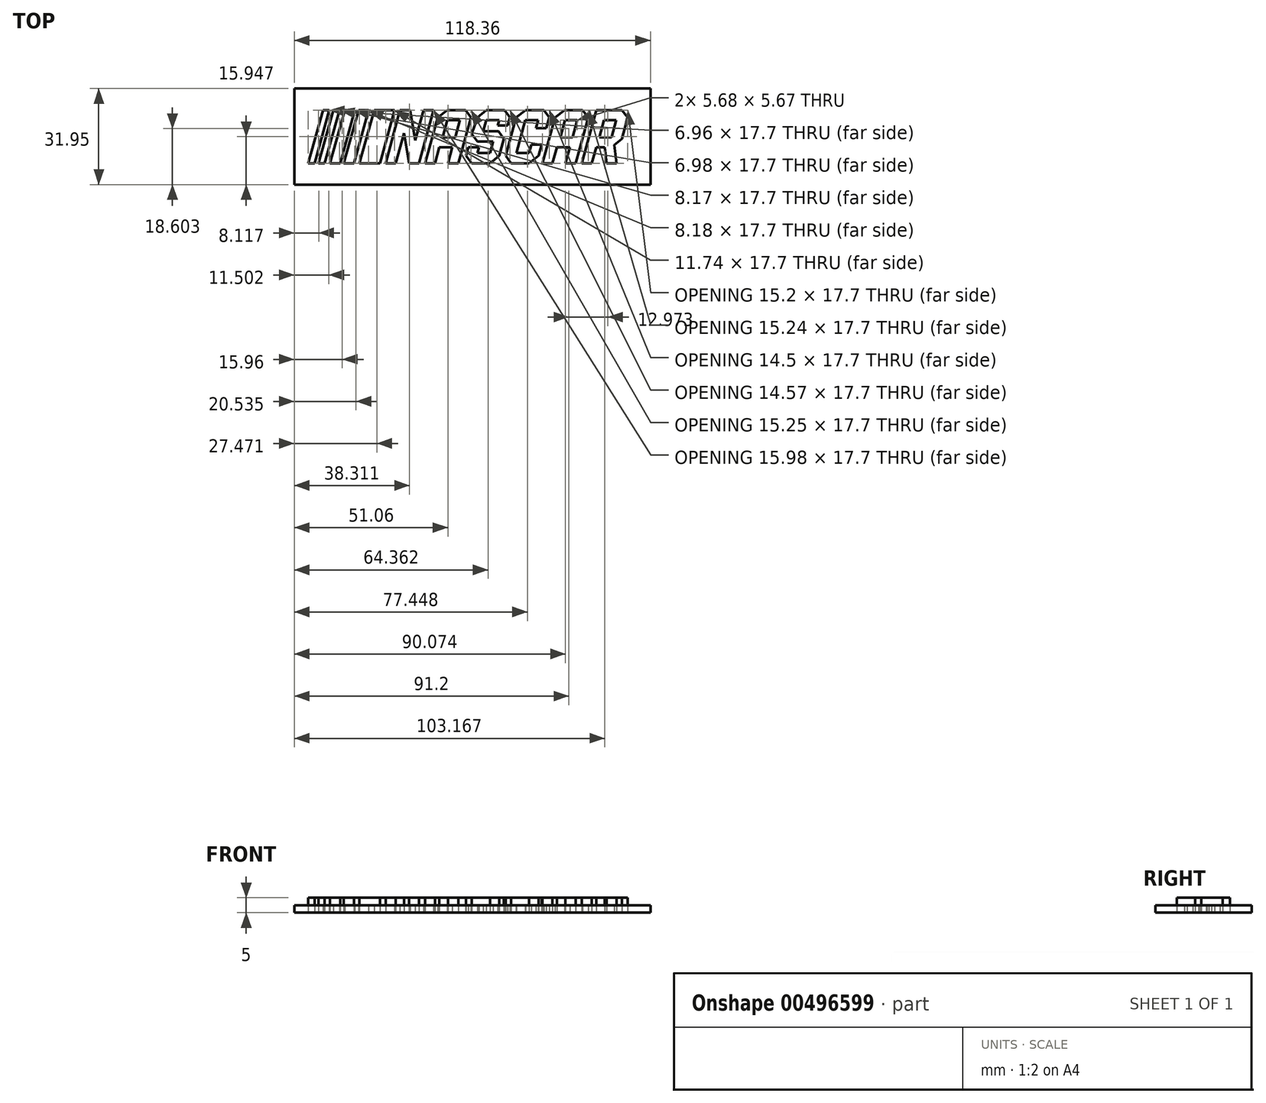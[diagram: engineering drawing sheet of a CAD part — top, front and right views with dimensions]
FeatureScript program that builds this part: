
annotation { "Feature Type Name" : "Feature", "Feature Type Description" : "" }
export const myFeature = defineFeature(function(context is Context, id is Id, definition is map)
    precondition{}
    {
        {
            var Q0;
            Q0=qCreatedBy(makeId("Top.planeOp"),FACE);
            var sketch = newSketch(context, id + "F0", { "sketchPlane" : qUnion([Q0])});
            skLineSegment(sketch, "E0", {"start": v(-60.8, 17.19) * mm, "end": v(-60.8, -14.75) * mm});
            skLineSegment(sketch, "E1", {"start": v(-60.8, -14.75) * mm, "end": v(57.56, -14.75) * mm});
            skLineSegment(sketch, "E2", {"start": v(57.56, -14.75) * mm, "end": v(57.56, 17.2) * mm});
            skLineSegment(sketch, "E3", {"start": v(57.56, 17.2) * mm, "end": v(-60.8, 17.19) * mm});
            skLineSegment(sketch, "E4", {"start": v(-51.25, 10.05) * mm, "end": v(-49.2, 10.05) * mm});
            skLineSegment(sketch, "E5", {"start": v(-49.2, 10.05) * mm, "end": v(-54.06, -7.65) * mm});
            skLineSegment(sketch, "E6", {"start": v(-54.06, -7.65) * mm, "end": v(-56.16, -7.65) * mm});
            skLineSegment(sketch, "E7", {"start": v(-56.16, -7.65) * mm, "end": v(-51.25, 10.05) * mm});
            skLineSegment(sketch, "E8", {"start": v(-47.86, 10.05) * mm, "end": v(-45.8, 10.05) * mm});
            skPoint(sketch, "E8.startSnap0", {"position": v(-50.23, 10.05) * mm});
            skLineSegment(sketch, "E9", {"start": v(-45.8, 10.05) * mm, "end": v(-50.73, -7.65) * mm});
            skLineSegment(sketch, "E10", {"start": v(-50.73, -7.65) * mm, "end": v(-52.79, -7.65) * mm});
            skLineSegment(sketch, "E11", {"start": v(-52.79, -7.65) * mm, "end": v(-47.86, 10.05) * mm});
            skLineSegment(sketch, "E12", {"start": v(-44, 10.05) * mm, "end": v(-40.75, 10.05) * mm});
            skLineSegment(sketch, "E13", {"start": v(-40.75, 10.05) * mm, "end": v(-45.6, -7.65) * mm});
            skLineSegment(sketch, "E14", {"start": v(-45.6, -7.65) * mm, "end": v(-48.93, -7.65) * mm});
            skLineSegment(sketch, "E15", {"start": v(-48.93, -7.65) * mm, "end": v(-44, 10.05) * mm});
            skLineSegment(sketch, "E16", {"start": v(-39.42, 10.05) * mm, "end": v(-36.17, 10.05) * mm});
            skLineSegment(sketch, "E17", {"start": v(-36.17, 10.05) * mm, "end": v(-41, -7.65) * mm});
            skLineSegment(sketch, "E18", {"start": v(-41, -7.65) * mm, "end": v(-44.35, -7.65) * mm});
            skLineSegment(sketch, "E19", {"start": v(-44.35, -7.65) * mm, "end": v(-39.42, 10.05) * mm});
            skLineSegment(sketch, "E20", {"start": v(-34.28, 10.05) * mm, "end": v(-27.46, 10.05) * mm});
            skPoint(sketch, "E20.startSnap0", {"position": v(-37.8, 10.05) * mm});
            skLineSegment(sketch, "E21", {"start": v(-27.46, 10.05) * mm, "end": v(-32.28, -7.65) * mm});
            skLineSegment(sketch, "E22", {"start": v(-32.28, -7.65) * mm, "end": v(-39.2, -7.65) * mm});
            skLineSegment(sketch, "E23", {"start": v(-39.2, -7.65) * mm, "end": v(-34.28, 10.05) * mm});
            skLineSegment(sketch, "E24", {"start": v(-25.65, 10.05) * mm, "end": v(-30.48, -7.65) * mm});
            skLineSegment(sketch, "E25", {"start": v(-30.48, -7.65) * mm, "end": v(-27.1, -7.65) * mm});
            skLineSegment(sketch, "E26", {"start": v(-27.1, -7.65) * mm, "end": v(-24.36, 2.43) * mm});
            skLineSegment(sketch, "E27", {"start": v(-24.36, 2.43) * mm, "end": v(-22.68, -7.65) * mm});
            skLineSegment(sketch, "E28", {"start": v(-22.68, -7.65) * mm, "end": v(-19.32, -7.65) * mm});
            skLineSegment(sketch, "E29", {"start": v(-19.32, -7.65) * mm, "end": v(-14.5, 10.05) * mm});
            skLineSegment(sketch, "E30", {"start": v(-14.5, 10.05) * mm, "end": v(-17.9, 10.05) * mm});
            skLineSegment(sketch, "E31", {"start": v(-17.9, 10.05) * mm, "end": v(-20.63, 0) * mm});
            skLineSegment(sketch, "E32", {"start": v(-20.63, 0) * mm, "end": v(-22.3, 10.05) * mm});
            skLineSegment(sketch, "E33", {"start": v(-22.3, 10.05) * mm, "end": v(-25.65, 10.05) * mm});
            skLineSegment(sketch, "E34", {"start": v(-9.95, 10.05) * mm, "end": v(-13.2, 7.63) * mm});
            skLineSegment(sketch, "E35", {"start": v(-13.2, 7.63) * mm, "end": v(-17.37, -7.65) * mm});
            skLineSegment(sketch, "E36", {"start": v(-17.37, -7.65) * mm, "end": v(-14.02, -7.65) * mm});
            skLineSegment(sketch, "E37", {"start": v(-14.02, -7.65) * mm, "end": v(-12.58, -2.35) * mm});
            skLineSegment(sketch, "E38", {"start": v(-12.58, -2.35) * mm, "end": v(-8.3, -2.35) * mm});
            skLineSegment(sketch, "E39", {"start": v(-8.3, -2.35) * mm, "end": v(-9.74, -7.65) * mm});
            skLineSegment(sketch, "E40", {"start": v(-9.74, -7.65) * mm, "end": v(-6.27, -7.65) * mm});
            skLineSegment(sketch, "E41", {"start": v(-6.27, -7.65) * mm, "end": v(-2.11, 7.6) * mm});
            skLineSegment(sketch, "E42", {"start": v(-2.11, 7.6) * mm, "end": v(-3.86, 10.05) * mm});
            skLineSegment(sketch, "E43", {"start": v(-3.86, 10.05) * mm, "end": v(-9.95, 10.05) * mm});
            skLineSegment(sketch, "E44", {"start": v(-9.95, 6.69) * mm, "end": v(-11.5, 1.02) * mm});
            skLineSegment(sketch, "E45", {"start": v(-11.5, 1.02) * mm, "end": v(-7.36, 1.02) * mm});
            skLineSegment(sketch, "E46", {"start": v(-7.36, 1.02) * mm, "end": v(-5.81, 6.72) * mm});
            skLineSegment(sketch, "E47", {"start": v(-5.81, 6.72) * mm, "end": v(-9.95, 6.69) * mm});
            skLineSegment(sketch, "E48", {"start": v(2.94, 10.05) * mm, "end": v(0, 7.6) * mm});
            skLineSegment(sketch, "E49", {"start": v(0, 7.6) * mm, "end": v(-1.78, 2.11) * mm});
            skLineSegment(sketch, "E50", {"start": v(-1.78, 2.11) * mm, "end": v(0, -0.4) * mm});
            skLineSegment(sketch, "E51", {"start": v(0, -0.4) * mm, "end": v(5.3, -0.4) * mm});
            skLineSegment(sketch, "E52", {"start": v(5.3, -0.4) * mm, "end": v(4.26, -4.24) * mm});
            skLineSegment(sketch, "E53", {"start": v(4.26, -4.24) * mm, "end": v(0, -4.24) * mm});
            skLineSegment(sketch, "E54", {"start": v(0, -4.24) * mm, "end": v(0.52, -2.35) * mm});
            skLineSegment(sketch, "E55", {"start": v(0.52, -2.35) * mm, "end": v(-2.97, -2.35) * mm});
            skLineSegment(sketch, "E56", {"start": v(-2.97, -2.35) * mm, "end": v(-3.72, -5.12) * mm});
            skLineSegment(sketch, "E57", {"start": v(-3.72, -5.12) * mm, "end": v(-1.78, -7.65) * mm});
            skLineSegment(sketch, "E58", {"start": v(-1.78, -7.65) * mm, "end": v(4.26, -7.65) * mm});
            skLineSegment(sketch, "E59", {"start": v(4.26, -7.65) * mm, "end": v(7.35, -5.12) * mm});
            skLineSegment(sketch, "E60", {"start": v(7.35, -5.12) * mm, "end": v(8.87, 0.46) * mm});
            skLineSegment(sketch, "E61", {"start": v(8.87, 0.46) * mm, "end": v(7.08, 2.96) * mm});
            skLineSegment(sketch, "E62", {"start": v(7.08, 2.96) * mm, "end": v(1.96, 2.96) * mm});
            skLineSegment(sketch, "E63", {"start": v(1.96, 2.96) * mm, "end": v(2.98, 6.69) * mm});
            skLineSegment(sketch, "E64", {"start": v(2.98, 6.69) * mm, "end": v(7.25, 6.69) * mm});
            skLineSegment(sketch, "E65", {"start": v(7.25, 6.69) * mm, "end": v(6.78, 4.94) * mm});
            skLineSegment(sketch, "E66", {"start": v(6.78, 4.94) * mm, "end": v(10.12, 4.94) * mm});
            skLineSegment(sketch, "E67", {"start": v(10.12, 4.94) * mm, "end": v(10.85, 7.6) * mm});
            skLineSegment(sketch, "E68", {"start": v(10.85, 7.6) * mm, "end": v(9.14, 10.05) * mm});
            skLineSegment(sketch, "E69", {"start": v(9.14, 10.05) * mm, "end": v(2.94, 10.05) * mm});
            skLineSegment(sketch, "E70", {"start": v(16.06, 10.05) * mm, "end": v(12.87, 7.6) * mm});
            skLineSegment(sketch, "E71", {"start": v(12.87, 7.6) * mm, "end": v(9.4, -5.12) * mm});
            skLineSegment(sketch, "E72", {"start": v(9.4, -5.12) * mm, "end": v(11.19, -7.65) * mm});
            skLineSegment(sketch, "E73", {"start": v(11.19, -7.65) * mm, "end": v(17.24, -7.65) * mm});
            skLineSegment(sketch, "E74", {"start": v(17.24, -7.65) * mm, "end": v(20.43, -5.12) * mm});
            skLineSegment(sketch, "E75", {"start": v(20.43, -5.12) * mm, "end": v(21.42, -1.5) * mm});
            skLineSegment(sketch, "E76", {"start": v(21.42, -1.5) * mm, "end": v(17.98, -1.5) * mm});
            skLineSegment(sketch, "E77", {"start": v(17.98, -1.5) * mm, "end": v(17.23, -4.24) * mm});
            skLineSegment(sketch, "E78", {"start": v(17.23, -4.24) * mm, "end": v(13, -4.24) * mm});
            skLineSegment(sketch, "E79", {"start": v(13, -4.24) * mm, "end": v(15.98, 6.69) * mm});
            skLineSegment(sketch, "E80", {"start": v(15.98, 6.69) * mm, "end": v(20.22, 6.69) * mm});
            skLineSegment(sketch, "E81", {"start": v(20.22, 6.69) * mm, "end": v(19.48, 3.97) * mm});
            skLineSegment(sketch, "E82", {"start": v(19.48, 3.97) * mm, "end": v(22.9, 3.97) * mm});
            skLineSegment(sketch, "E83", {"start": v(22.9, 3.97) * mm, "end": v(23.9, 7.6) * mm});
            skLineSegment(sketch, "E84", {"start": v(23.9, 7.6) * mm, "end": v(22.18, 10.05) * mm});
            skLineSegment(sketch, "E85", {"start": v(22.18, 10.05) * mm, "end": v(16.06, 10.05) * mm});
            skLineSegment(sketch, "E86", {"start": v(29, 10.05) * mm, "end": v(25.81, 7.6) * mm});
            skLineSegment(sketch, "E87", {"start": v(25.81, 7.6) * mm, "end": v(21.65, -7.65) * mm});
            skLineSegment(sketch, "E88", {"start": v(21.65, -7.65) * mm, "end": v(25, -7.65) * mm});
            skLineSegment(sketch, "E89", {"start": v(25, -7.65) * mm, "end": v(26.45, -2.35) * mm});
            skLineSegment(sketch, "E90", {"start": v(26.45, -2.35) * mm, "end": v(30.75, -2.35) * mm});
            skLineSegment(sketch, "E91", {"start": v(30.75, -2.35) * mm, "end": v(29.3, -7.65) * mm});
            skLineSegment(sketch, "E92", {"start": v(29.3, -7.65) * mm, "end": v(32.74, -7.65) * mm});
            skLineSegment(sketch, "E93", {"start": v(32.74, -7.65) * mm, "end": v(36.9, 7.6) * mm});
            skLineSegment(sketch, "E94", {"start": v(36.9, 7.6) * mm, "end": v(35.03, 10.05) * mm});
            skLineSegment(sketch, "E95", {"start": v(35.03, 10.05) * mm, "end": v(29, 10.05) * mm});
            skLineSegment(sketch, "E96", {"start": v(33.24, 6.69) * mm, "end": v(31.7, 1.02) * mm});
            skLineSegment(sketch, "E97", {"start": v(31.7, 1.02) * mm, "end": v(27.56, 1.02) * mm});
            skLineSegment(sketch, "E98", {"start": v(27.56, 1.02) * mm, "end": v(29.1, 6.69) * mm});
            skLineSegment(sketch, "E99", {"start": v(29.1, 6.69) * mm, "end": v(33.24, 6.69) * mm});
            skLineSegment(sketch, "E100", {"start": v(39.6, 10.05) * mm, "end": v(34.77, -7.65) * mm});
            skLineSegment(sketch, "E101", {"start": v(34.77, -7.65) * mm, "end": v(38.07, -7.65) * mm});
            skLineSegment(sketch, "E102", {"start": v(38.07, -7.65) * mm, "end": v(39.52, -2.35) * mm});
            skLineSegment(sketch, "E103", {"start": v(39.52, -2.35) * mm, "end": v(42.33, -2.35) * mm});
            skLineSegment(sketch, "E104", {"start": v(42.33, -2.35) * mm, "end": v(42.94, -7.65) * mm});
            skLineSegment(sketch, "E105", {"start": v(42.94, -7.65) * mm, "end": v(46.3, -7.65) * mm});
            skLineSegment(sketch, "E106", {"start": v(46.3, -7.65) * mm, "end": v(45.56, -1.6) * mm});
            skLineSegment(sketch, "E107", {"start": v(45.56, -1.6) * mm, "end": v(48.02, 0.46) * mm});
            skLineSegment(sketch, "E108", {"start": v(48.02, 0.46) * mm, "end": v(49.97, 7.6) * mm});
            skLineSegment(sketch, "E109", {"start": v(49.97, 7.6) * mm, "end": v(48.1, 10.05) * mm});
            skLineSegment(sketch, "E110", {"start": v(48.1, 10.05) * mm, "end": v(39.6, 10.05) * mm});
            skLineSegment(sketch, "E111", {"start": v(42.06, 6.69) * mm, "end": v(46.21, 6.69) * mm});
            skLineSegment(sketch, "E112", {"start": v(46.21, 6.69) * mm, "end": v(44.67, 1.02) * mm});
            skLineSegment(sketch, "E113", {"start": v(44.67, 1.02) * mm, "end": v(40.53, 1.02) * mm});
            skLineSegment(sketch, "E114", {"start": v(40.53, 1.02) * mm, "end": v(42.06, 6.69) * mm});
            skSolve(sketch);
        }
        {
            var Q0;
            Q0=makeQuery(id+"F0.imprint","IMPRINT",FACE,{"disambiguationData":[TD([[makeQuery(id+"F0.imprint","IMPRINT",EDGE,{"derivedFrom":sQuery(id+"F0.wireOp",EDGE,"E4")}),-1.0]])]});
            var Q1;
            Q1=makeQuery(id+"F0.imprint","IMPRINT",FACE,{"disambiguationData":[TD([[makeQuery(id+"F0.imprint","IMPRINT",EDGE,{"derivedFrom":sQuery(id+"F0.wireOp",EDGE,"E8")}),-1.0]])]});
            var Q2;
            Q2=makeQuery(id+"F0.imprint","IMPRINT",FACE,{"disambiguationData":[TD([[makeQuery(id+"F0.imprint","IMPRINT",EDGE,{"derivedFrom":sQuery(id+"F0.wireOp",EDGE,"E12")}),-1.0]])]});
            var Q3;
            Q3=makeQuery(id+"F0.imprint","IMPRINT",FACE,{"disambiguationData":[TD([[makeQuery(id+"F0.imprint","IMPRINT",EDGE,{"derivedFrom":sQuery(id+"F0.wireOp",EDGE,"E16")}),-1.0]])]});
            var Q4;
            Q4=makeQuery(id+"F0.imprint","IMPRINT",FACE,{"disambiguationData":[TD([[makeQuery(id+"F0.imprint","IMPRINT",EDGE,{"derivedFrom":sQuery(id+"F0.wireOp",EDGE,"E20")}),-1.0]])]});
            var Q5;
            Q5=makeQuery(id+"F0.imprint","IMPRINT",FACE,{"disambiguationData":[TD([[makeQuery(id+"F0.imprint","IMPRINT",EDGE,{"derivedFrom":sQuery(id+"F0.wireOp",EDGE,"E24")}),1.0]])]});
            var Q6;
            Q6=makeQuery(id+"F0.imprint","IMPRINT",FACE,{"disambiguationData":[TD([[makeQuery(id+"F0.imprint","IMPRINT",EDGE,{"derivedFrom":sQuery(id+"F0.wireOp",EDGE,"E34")}),1.0]])]});
            var Q7;
            Q7=makeQuery(id+"F0.imprint","IMPRINT",FACE,{"disambiguationData":[TD([[makeQuery(id+"F0.imprint","IMPRINT",EDGE,{"derivedFrom":sQuery(id+"F0.wireOp",EDGE,"E48")}),1.0]])]});
            var Q8;
            Q8=makeQuery(id+"F0.imprint","IMPRINT",FACE,{"disambiguationData":[TD([[makeQuery(id+"F0.imprint","IMPRINT",EDGE,{"derivedFrom":sQuery(id+"F0.wireOp",EDGE,"E70")}),1.0]])]});
            var Q9;
            Q9=makeQuery(id+"F0.imprint","IMPRINT",FACE,{"disambiguationData":[TD([[makeQuery(id+"F0.imprint","IMPRINT",EDGE,{"derivedFrom":sQuery(id+"F0.wireOp",EDGE,"E86")}),1.0]])]});
            var Q10;
            Q10=makeQuery(id+"F0.imprint","IMPRINT",FACE,{"disambiguationData":[TD([[makeQuery(id+"F0.imprint","IMPRINT",EDGE,{"derivedFrom":sQuery(id+"F0.wireOp",EDGE,"E100")}),1.0]])]});
            extrude(context, id + "F1", {"entities" : qUnion([Q0, Q1, Q2, Q3, Q4, Q5, Q6, Q7, Q8, Q9, Q10]), "depth" : 5 * mm, "offsetDistance" : 25 * mm});
        }
        {
            var Q0;
            Q0=makeQuery(id+"F0.imprint","IMPRINT",FACE,{"disambiguationData":[TD([[makeQuery(id+"F0.imprint","IMPRINT",EDGE,{"derivedFrom":sQuery(id+"F0.wireOp",EDGE,"E0")}),1.0]])]});
            extrude(context, id + "F2", {"entities" : qUnion([Q0]), "depth" : 2.5 * mm, "offsetDistance" : 25 * mm});
        }
    });
